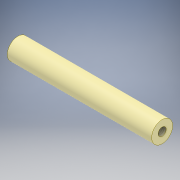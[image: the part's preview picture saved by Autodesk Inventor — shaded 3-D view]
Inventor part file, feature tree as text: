
AUTODESK INVENTOR PART (.ipt)
format: ipt  version: 2018 (Build 220112000, 112)  size: 96,768 bytes
history: native  units: mm
features: extrude x1, hole x1, sketch x1
ambient origin geometry x8: Origin, YZ Plane, XZ Plane, XY Plane, X Axis, Y Axis, Z Axis, Center Point
bodies: Solid1 (feature_tree)
feature tree (3):
  extrude  "Extrusion1"  Depth=87.3mm TaperAngle=0.0deg
  hole  "Hole1"  [1 undecoded]
  sketch  "Sketch1"  dims[d0=12.7mm d1=87.3mm d2=0.0mm d3=10.0mm d4=10.0mm d5=4.917mm d6=12.0mm d7=4.0mm d8=2.0mm d9=90.0deg d10=17.1mm d11=20.594885mm]
note: 1 required parameter value undecoded (feature->parameter linkage not recoverable at this tier; creation-order binding heuristic only, values carry confidence <= 0.55)
